# Revit family: RN 80021 Optipress-Aquaplus-Réduction
name_source: partatom
category: Rohrformteile
units: mm (PartAtom-declared; Revit-internal decimal feet)

## family parameters
Arbeitsebenenbasiert = Nein
Beim Laden mit Abzugskörper schneiden = Nein
Bemaßung runder Anschluss = Durchmesser verwenden
Gemeinsam genutzt = Ja
Immer vertikal = Ja
OmniClass-Nummer = 23.60.30.11.14
OmniClass-Titel = Pipework Fittings
Teiletyp = Übergang

## types (2) — shared parameters
Beschreibung = Reduzierstück
Hersteller = R. Nussbaum AG
IfcDescription = Reduzierstück
IfcExportAs = IfcPipeFitting
IfcExportType = TRANSITION
Modell = 0
RN_LOD = LOD 400
RN_Manufactur = R. Nussbaum AG
RN_Mat = Edelstahl 1.4401
RN_Serie = Optipress Aquaplus
RN_tab = RN_80021
URL = https://www.nussbaum.ch

## per-type parameters (varying)
| type | Bauelement | RN_Muffe | Typenkommentare |
| mit Muffe | 03.01.07.03 | Ja | Optipress-Aquaplus-Réductionmit Muffe |
| ohne Muffe |  | Nein | Optipress-Aquaplus-Réductionohne Muffe |

## geometry (parser evidence)
native form markers: Sweep x2
no freeform markers — native parametric forms only
